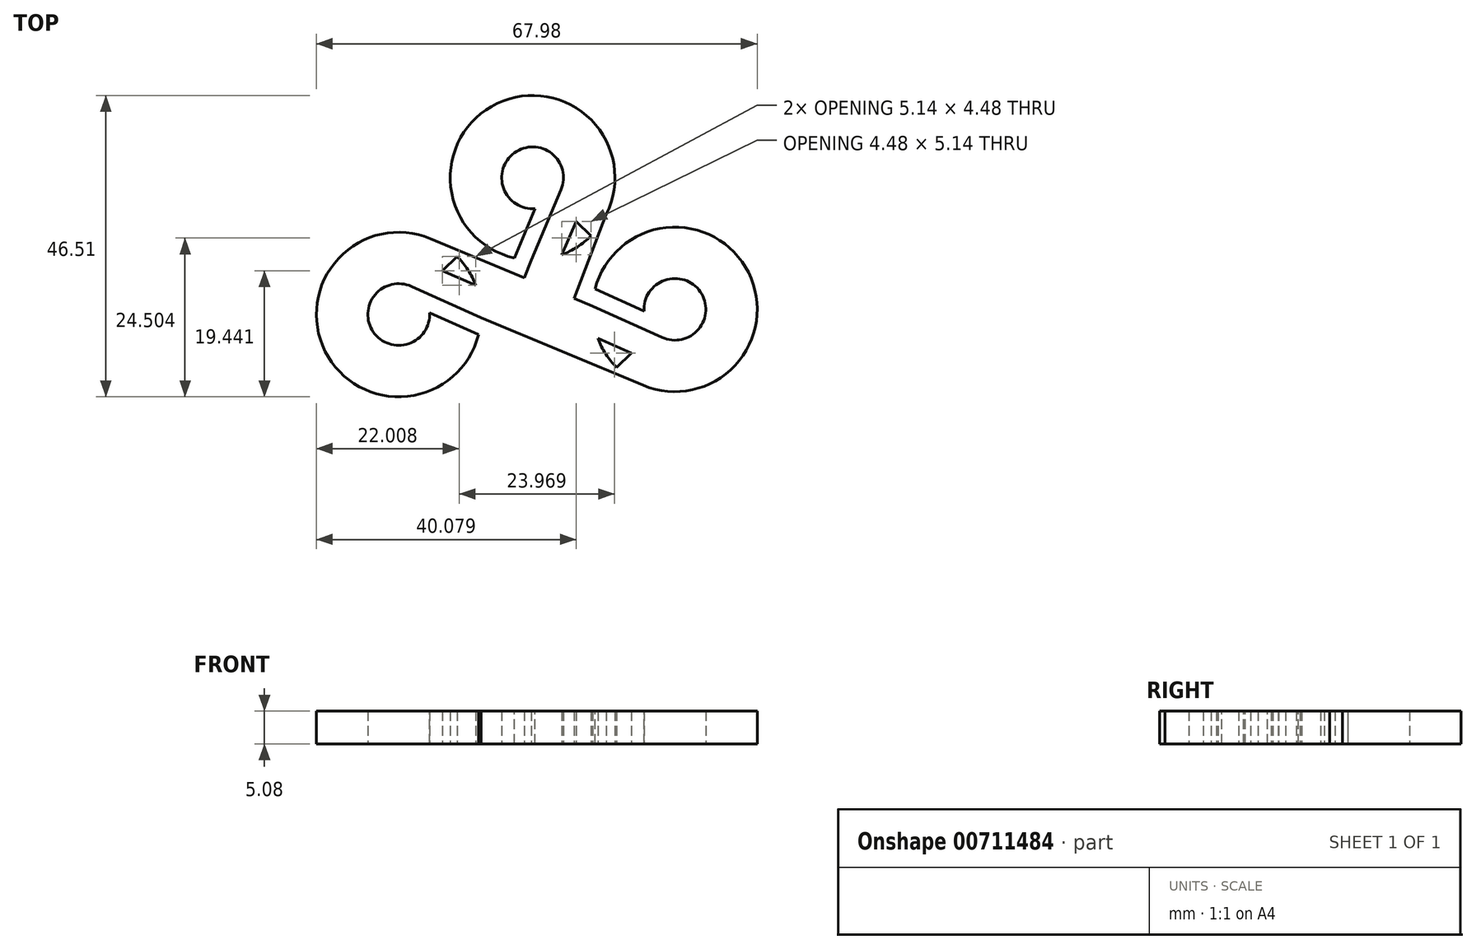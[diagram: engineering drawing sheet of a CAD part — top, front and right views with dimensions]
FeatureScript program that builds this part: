
annotation { "Feature Type Name" : "Feature", "Feature Type Description" : "" }
export const myFeature = defineFeature(function(context is Context, id is Id, definition is map)
    precondition{}
    {
        {
            var Q0;
            Q0=qCreatedBy(makeId("Top.planeOp"),FACE);
            var sketch = newSketch(context, id + "F0", { "sketchPlane" : qUnion([Q0])});
            skCircle(sketch, "E0", {"center": v(0, 0) * mm, "radius": 12.7 * mm});
            skCircle(sketch, "E1", {"center": v(21.94, -20.3) * mm, "radius": 12.7 * mm});
            skCircle(sketch, "E2", {"center": v(-20.64, -21.1) * mm, "radius": 12.7 * mm});
            skLineSegment(sketch, "E3", {"start": v(21.94, -20.3) * mm, "end": v(21.94, -33) * mm});
            skLineSegment(sketch, "E4", {"start": v(0, 0) * mm, "end": v(0, -12.7) * mm});
            skLineSegment(sketch, "E5", {"start": v(0, 0) * mm, "end": v(8.98, -8.98) * mm});
            skLineSegment(sketch, "E6", {"start": v(21.94, -20.3) * mm, "end": v(12.96, -29.29) * mm});
            skCircle(sketch, "E7", {"center": v(21.94, -20.3) * mm, "radius": 4.76 * mm});
            skLineSegment(sketch, "E8", {"start": v(21.94, -20.3) * mm, "end": v(17.45, -24.8) * mm});
            skCircle(sketch, "E9", {"center": v(0, 0) * mm, "radius": 4.76 * mm});
            skLineSegment(sketch, "E10", {"start": v(0, 0) * mm, "end": v(4.5, -4.5) * mm});
            skLineSegment(sketch, "E11", {"start": v(-20.64, -21.1) * mm, "end": v(-11.66, -12.13) * mm});
            skCircle(sketch, "E12", {"center": v(-20.64, -21.1) * mm, "radius": 4.76 * mm});
            skLineSegment(sketch, "E13", {"start": v(-20.64, -21.1) * mm, "end": v(-7.94, -21.1) * mm});
            skLineSegment(sketch, "E14", {"start": v(17.45, -24.8) * mm, "end": v(12.96, -29.29) * mm});
            skLineSegment(sketch, "E15", {"start": v(12.96, -29.29) * mm, "end": v(15.2, -27.04) * mm});
            skLineSegment(sketch, "E16", {"start": v(4.5, -4.5) * mm, "end": v(8.98, -8.98) * mm});
            skLineSegment(sketch, "E17", {"start": v(-16.15, -16.62) * mm, "end": v(-11.66, -12.13) * mm});
            skLineSegment(sketch, "E18", {"start": v(-17.27, -17.74) * mm, "end": v(17.06, -32.03) * mm});
            skLineSegment(sketch, "E19", {"start": v(18.58, -23.68) * mm, "end": v(-15.76, -9.38) * mm});
            skLineSegment(sketch, "E20", {"start": v(3.37, -3.37) * mm, "end": v(-1.24, -15.43) * mm});
            skLineSegment(sketch, "E21", {"start": v(-17.27, -17.74) * mm, "end": v(-13.9, -14.37) * mm});
            skLineSegment(sketch, "E22", {"start": v(-13.9, -14.37) * mm, "end": v(15.2, -27.04) * mm});
            skLineSegment(sketch, "E23", {"start": v(6.74, -6.74) * mm, "end": v(0.65, -20.7) * mm});
            skLineSegment(sketch, "E24", {"start": v(11.39, -5.62) * mm, "end": v(6.42, -18.62) * mm});
            skSolve(sketch);
        }
        {
            var Q0;
            Q0 = qSketchRegion(id + "F0", true);
            var Q1;
            {var subQ0=sQuery(id+"F0.wireOp",EDGE,"yDXB3k3o-TFvE-FYoA-wN1f-QkH4QK7AQUMg");var subQ1=sQuery(id+"F0.wireOp",EDGE,"E0");var subQ2=makeQuery(id+"F0.imprint","INTERSECT",VERTEX,{"derivedFrom":[subQ1,subQ0]});Q1=makeQuery(id+"F0.imprint","IMPRINT",FACE,{"disambiguationData":[TD([[makeQuery(id+"F0.imprint","IMPRINT",EDGE,{"disambiguationData":[TD([[subQ2,-1.0]])],"derivedFrom":subQ1}),1.0]])]});}
            var Q2;
            {var subQ0=sQuery(id+"F0.wireOp",EDGE,"E17");var subQ3=sQuery(id+"F0.wireOp",EDGE,"J90078Zz-WnI3-3mMf-xPuW-VheWCmXxd4jc");var subQ5=makeQuery(id+"F0.imprint","INTERSECT",VERTEX,{"derivedFrom":[subQ0,subQ3]});Q2=makeQuery(id+"F0.imprint","IMPRINT",FACE,{"disambiguationData":[TD([[makeQuery(id+"F0.imprint","IMPRINT",EDGE,{"disambiguationData":[TD([[subQ5,-1.0]])],"derivedFrom":subQ3}),1.0]])]});}
            var Q3;
            {var subQ0=sQuery(id+"F0.wireOp",EDGE,"E16");var subQ3=sQuery(id+"F0.wireOp",EDGE,"qBhyJChg-6HFi-ImKc-3mO0-xAAPeeJnZw3U");var subQ5=makeQuery(id+"F0.imprint","INTERSECT",VERTEX,{"derivedFrom":[subQ0,subQ3]});Q3=makeQuery(id+"F0.imprint","IMPRINT",FACE,{"disambiguationData":[TD([[makeQuery(id+"F0.imprint","IMPRINT",EDGE,{"disambiguationData":[TD([[subQ5,-1.0]])],"derivedFrom":subQ3}),1.0]])]});}
            var Q4;
            {var subQ0=sQuery(id+"F0.wireOp",EDGE,"E15");Q4=makeQuery(id+"F0.imprint","IMPRINT",FACE,{"disambiguationData":[TD([[makeQuery(id+"F0.imprint","IMPRINT",EDGE,{"derivedFrom":subQ0}),1.0]])]});}
            var Q5;
            {var subQ0=sQuery(id+"F0.wireOp",EDGE,"uzKKBWqX-qUkN-Bwqt-uPOb-Zz89Ibqqk1gW");var subQ1=sQuery(id+"F0.wireOp",EDGE,"E2");var subQ2=makeQuery(id+"F0.imprint","INTERSECT",VERTEX,{"derivedFrom":[subQ1,subQ0]});Q5=makeQuery(id+"F0.imprint","IMPRINT",FACE,{"disambiguationData":[TD([[makeQuery(id+"F0.imprint","IMPRINT",EDGE,{"disambiguationData":[TD([[subQ2,-1.0]])],"derivedFrom":subQ1}),-1.0]])]});}
            var Q6;
            {var subQ0=sQuery(id+"F0.wireOp",EDGE,"bYxaBZOP-HbRW-pdFW-15Ub-mmeAeTIA2QFz");Q6=makeQuery(id+"F0.imprint","IMPRINT",FACE,{"disambiguationData":[TD([[makeQuery(id+"F0.imprint","IMPRINT",EDGE,{"derivedFrom":subQ0}),-1.0]])]});}
            var Q7;
            {var subQ0=sQuery(id+"F0.wireOp",EDGE,"uzKKBWqX-qUkN-Bwqt-uPOb-Zz89Ibqqk1gW");var subQ1=sQuery(id+"F0.wireOp",EDGE,"E2");var subQ2=makeQuery(id+"F0.imprint","INTERSECT",VERTEX,{"derivedFrom":[subQ1,subQ0]});Q7=makeQuery(id+"F0.imprint","IMPRINT",FACE,{"disambiguationData":[TD([[makeQuery(id+"F0.imprint","IMPRINT",EDGE,{"disambiguationData":[TD([[subQ2,-1.0]])],"derivedFrom":subQ1}),1.0]])]});}
            var Q8;
            {var subQ0=sQuery(id+"F0.wireOp",EDGE,"Z3ejKgqz-Hqn6-uIZ8-Rk3e-6zc6qRlB8dJ0");Q8=makeQuery(id+"F0.imprint","IMPRINT",FACE,{"disambiguationData":[TD([[makeQuery(id+"F0.imprint","IMPRINT",EDGE,{"derivedFrom":subQ0}),-1.0]])]});}
            var Q9;
            {var subQ1=sQuery(id+"F0.wireOp",EDGE,"E0");var subQ3=sQuery(id+"F0.wireOp",EDGE,"qBhyJChg-6HFi-ImKc-3mO0-xAAPeeJnZw3U");var subQ4=makeQuery(id+"F0.imprint","INTERSECT",VERTEX,{"derivedFrom":[subQ1,subQ3]});Q9=makeQuery(id+"F0.imprint","IMPRINT",FACE,{"disambiguationData":[TD([[makeQuery(id+"F0.imprint","IMPRINT",EDGE,{"disambiguationData":[TD([[subQ4,-1.0]])],"derivedFrom":subQ3}),1.0]])]});}
            var Q10;
            {var subQ3=sQuery(id+"F0.wireOp",EDGE,"E0");var subQ5=sQuery(id+"F0.wireOp",EDGE,"E4");var subQ6=makeQuery(id+"F0.imprint","INTERSECT",VERTEX,{"derivedFrom":[subQ3,subQ5]});Q10=makeQuery(id+"F0.imprint","IMPRINT",FACE,{"disambiguationData":[TD([[makeQuery(id+"F0.imprint","IMPRINT",EDGE,{"disambiguationData":[TD([[subQ6,-1.0]])],"derivedFrom":subQ3}),1.0]])]});}
            var Q11;
            {var subQ0=sQuery(id+"F0.wireOp",EDGE,"yDXB3k3o-TFvE-FYoA-wN1f-QkH4QK7AQUMg");var subQ1=sQuery(id+"F0.wireOp",EDGE,"E0");var subQ2=makeQuery(id+"F0.imprint","INTERSECT",VERTEX,{"derivedFrom":[subQ1,subQ0]});Q11=makeQuery(id+"F0.imprint","IMPRINT",FACE,{"disambiguationData":[TD([[makeQuery(id+"F0.imprint","IMPRINT",EDGE,{"disambiguationData":[TD([[subQ2,-1.0]])],"derivedFrom":subQ1}),-1.0]])]});}
            var Q12;
            {var subQ0=sQuery(id+"F0.wireOp",EDGE,"Z3ejKgqz-Hqn6-uIZ8-Rk3e-6zc6qRlB8dJ0");Q12=makeQuery(id+"F0.imprint","IMPRINT",FACE,{"disambiguationData":[TD([[makeQuery(id+"F0.imprint","IMPRINT",EDGE,{"derivedFrom":subQ0}),1.0]])]});}
            var Q13;
            {var subQ0=sQuery(id+"F0.wireOp",EDGE,"6yfvUeka-AtBQ-0gim-mu1m-la48lc1LBtnG");var subQ5=sQuery(id+"F0.wireOp",EDGE,"qBhyJChg-6HFi-ImKc-3mO0-xAAPeeJnZw3U");var subQ6=makeQuery(id+"F0.imprint","INTERSECT",VERTEX,{"derivedFrom":[subQ0,subQ5]});Q13=makeQuery(id+"F0.imprint","IMPRINT",FACE,{"disambiguationData":[TD([[makeQuery(id+"F0.imprint","IMPRINT",EDGE,{"disambiguationData":[TD([[subQ6,1.0]])],"derivedFrom":subQ5}),-1.0]])]});}
            var Q14;
            {var subQ0=sQuery(id+"F0.wireOp",EDGE,"6yfvUeka-AtBQ-0gim-mu1m-la48lc1LBtnG");var subQ5=sQuery(id+"F0.wireOp",EDGE,"qBhyJChg-6HFi-ImKc-3mO0-xAAPeeJnZw3U");var subQ6=makeQuery(id+"F0.imprint","INTERSECT",VERTEX,{"derivedFrom":[subQ0,subQ5]});Q14=makeQuery(id+"F0.imprint","IMPRINT",FACE,{"disambiguationData":[TD([[makeQuery(id+"F0.imprint","IMPRINT",EDGE,{"disambiguationData":[TD([[subQ6,1.0]])],"derivedFrom":subQ5}),1.0]])]});}
            var Q15;
            {var subQ0=sQuery(id+"F0.wireOp",EDGE,"z5MUbxWM-Vo3r-AQEv-g91w-RWlkdqbgf4P1");Q15=makeQuery(id+"F0.imprint","IMPRINT",FACE,{"disambiguationData":[TD([[makeQuery(id+"F0.imprint","IMPRINT",EDGE,{"derivedFrom":subQ0}),-1.0]])]});}
            var Q16;
            {var subQ1=sQuery(id+"F0.wireOp",EDGE,"E12");var subQ3=sQuery(id+"F0.wireOp",EDGE,"E13");var subQ4=makeQuery(id+"F0.imprint","INTERSECT",VERTEX,{"derivedFrom":[subQ1,subQ3]});Q16=makeQuery(id+"F0.imprint","IMPRINT",FACE,{"disambiguationData":[TD([[makeQuery(id+"F0.imprint","IMPRINT",EDGE,{"disambiguationData":[TD([[subQ4,-1.0]])],"derivedFrom":subQ3}),1.0]])]});}
            var Q17;
            {var subQ3=sQuery(id+"F0.wireOp",EDGE,"E2");var subQ7=sQuery(id+"F0.wireOp",EDGE,"E13");var subQ8=makeQuery(id+"F0.imprint","INTERSECT",VERTEX,{"derivedFrom":[subQ3,subQ7]});Q17=makeQuery(id+"F0.imprint","IMPRINT",FACE,{"disambiguationData":[TD([[makeQuery(id+"F0.imprint","IMPRINT",EDGE,{"disambiguationData":[TD([[subQ8,-1.0]])],"derivedFrom":subQ3}),1.0]])]});}
            var Q18;
            {var subQ5=sQuery(id+"F0.wireOp",EDGE,"E14");Q18=makeQuery(id+"F0.imprint","IMPRINT",FACE,{"disambiguationData":[TD([[makeQuery(id+"F0.imprint","IMPRINT",EDGE,{"derivedFrom":subQ5}),-1.0]])]});}
            var Q19;
            {var subQ0=sQuery(id+"F0.wireOp",EDGE,"NG6Fn4Pl-cfwn-nJXz-Nv7R-ltP6G86gKaW2");var subQ1=sQuery(id+"F0.wireOp",EDGE,"E1");var subQ2=makeQuery(id+"F0.imprint","INTERSECT",VERTEX,{"derivedFrom":[subQ1,subQ0]});Q19=makeQuery(id+"F0.imprint","IMPRINT",FACE,{"disambiguationData":[TD([[makeQuery(id+"F0.imprint","IMPRINT",EDGE,{"disambiguationData":[TD([[subQ2,-1.0]])],"derivedFrom":subQ1}),-1.0]])]});}
            var Q20;
            {var subQ0=sQuery(id+"F0.wireOp",EDGE,"bYxaBZOP-HbRW-pdFW-15Ub-mmeAeTIA2QFz");Q20=makeQuery(id+"F0.imprint","IMPRINT",FACE,{"disambiguationData":[TD([[makeQuery(id+"F0.imprint","IMPRINT",EDGE,{"derivedFrom":subQ0}),1.0]])]});}
            var Q21;
            {var subQ1=sQuery(id+"F0.wireOp",EDGE,"z5MUbxWM-Vo3r-AQEv-g91w-RWlkdqbgf4P1");Q21=makeQuery(id+"F0.imprint","IMPRINT",FACE,{"disambiguationData":[TD([[makeQuery(id+"F0.imprint","IMPRINT",EDGE,{"derivedFrom":subQ1}),1.0]])]});}
            var Q22;
            {var subQ0=sQuery(id+"F0.wireOp",EDGE,"eJoCJf4v-nHHx-lm19-L27D-6VjAbPNY3byg");var subQ1=sQuery(id+"F0.wireOp",EDGE,"E2");var subQ2=makeQuery(id+"F0.imprint","INTERSECT",VERTEX,{"derivedFrom":[subQ1,subQ0]});Q22=makeQuery(id+"F0.imprint","IMPRINT",FACE,{"disambiguationData":[TD([[makeQuery(id+"F0.imprint","IMPRINT",EDGE,{"disambiguationData":[TD([[subQ2,-1.0]])],"derivedFrom":subQ1}),1.0]])]});}
            var Q23;
            {var subQ0=sQuery(id+"F0.wireOp",EDGE,"E9");var subQ1=sQuery(id+"F0.wireOp",EDGE,"E4");var subQ2=makeQuery(id+"F0.imprint","INTERSECT",VERTEX,{"derivedFrom":[subQ1,subQ0]});Q23=makeQuery(id+"F0.imprint","IMPRINT",FACE,{"disambiguationData":[TD([[makeQuery(id+"F0.imprint","IMPRINT",EDGE,{"disambiguationData":[TD([[subQ2,-1.0]])],"derivedFrom":subQ1}),1.0]])]});}
            var Q24;
            {var subQ0=sQuery(id+"F0.wireOp",EDGE,"E17");Q24=makeQuery(id+"F0.imprint","IMPRINT",FACE,{"disambiguationData":[TD([[makeQuery(id+"F0.imprint","IMPRINT",EDGE,{"derivedFrom":subQ0}),-1.0]])]});}
            var Q25;
            {var subQ0=sQuery(id+"F0.wireOp",EDGE,"E16");var subQ1=sQuery(id+"F0.wireOp",EDGE,"E0");var subQ2=makeQuery(id+"F0.imprint","INTERSECT",VERTEX,{"derivedFrom":[subQ1,subQ0]});Q25=makeQuery(id+"F0.imprint","IMPRINT",FACE,{"disambiguationData":[TD([[makeQuery(id+"F0.imprint","IMPRINT",EDGE,{"disambiguationData":[TD([[subQ2,1.0]])],"derivedFrom":subQ1}),1.0]])]});}
            extrude(context, id + "F1", {"entities" : qUnion([Q0, Q1, Q2, Q3, Q4, Q5, Q6, Q7, Q8, Q9, Q10, Q11, Q12, Q13, Q14, Q15, Q16, Q17, Q18, Q19, Q20, Q21, Q22, Q23, Q24, Q25]), "depth" : 5.08 * mm, "offsetDistance" : 25.4 * mm});
        }
        {
            var Q0;
            Q0=makeQuery(id+"F1.opExtrude","CAP_FACE",FACE,{"disambiguationData":[OSD([sQuery(id+"F0.wireOp",EDGE,"E0"),sQuery(id+"F0.wireOp",EDGE,"E1"),sQuery(id+"F0.wireOp",EDGE,"E2"),sQuery(id+"F0.wireOp",EDGE,"VeAweMac-LZ9O-rFIa-PTyz-U5xl3IZNd5pn"),sQuery(id+"F0.wireOp",EDGE,"E7"),sQuery(id+"F0.wireOp",EDGE,"NG6Fn4Pl-cfwn-nJXz-Nv7R-ltP6G86gKaW2"),sQuery(id+"F0.wireOp",EDGE,"E9"),sQuery(id+"F0.wireOp",EDGE,"yDXB3k3o-TFvE-FYoA-wN1f-QkH4QK7AQUMg"),sQuery(id+"F0.wireOp",EDGE,"6yfvUeka-AtBQ-0gim-mu1m-la48lc1LBtnG"),sQuery(id+"F0.wireOp",EDGE,"E12"),sQuery(id+"F0.wireOp",EDGE,"uzKKBWqX-qUkN-Bwqt-uPOb-Zz89Ibqqk1gW"),sQuery(id+"F0.wireOp",EDGE,"z5MUbxWM-Vo3r-AQEv-g91w-RWlkdqbgf4P1"),sQuery(id+"F0.wireOp",EDGE,"qBhyJChg-6HFi-ImKc-3mO0-xAAPeeJnZw3U"),sQuery(id+"F0.wireOp",EDGE,"Vy6klFHD-ql6F-NG0b-UYJ5-acndccB01QWS"),sQuery(id+"F0.wireOp",EDGE,"OdPr5M7K-QP7o-Xsb9-YXNN-OMWYOfSv6xGX"),sQuery(id+"F0.wireOp",EDGE,"tfzjCEgK-RNZ7-z4IH-43NG-UBwa0SwhfyJe")])],"isStart":false});
            var sketch = newSketch(context, id + "F2", { "sketchPlane" : qUnion([Q0])});
            skLineSegment(sketch, "E25", {"start": v(-0.2, -12.7) * mm, "end": v(4.39, -1.86) * mm});
            skLineSegment(sketch, "E26", {"start": v(-2.82, -12.38) * mm, "end": v(0.4, -4.75) * mm});
            skLineSegment(sketch, "E27", {"start": v(-7.95, -21.62) * mm, "end": v(-18.68, -16.77) * mm});
            skLineSegment(sketch, "E28", {"start": v(-15.88, -20.82) * mm, "end": v(-8.33, -24.24) * mm});
            skLineSegment(sketch, "E29", {"start": v(9.25, -19.8) * mm, "end": v(19.98, -24.65) * mm});
            skLineSegment(sketch, "E30", {"start": v(9.63, -17.18) * mm, "end": v(17.19, -20.6) * mm});
            skSolve(sketch);
        }
        {
            var Q0;
            {var subQ0=sQuery(id+"F2.wireOp",EDGE,"E27");Q0=makeQuery(id+"F2.imprint","IMPRINT",FACE,{"disambiguationData":[TD([[makeQuery(id+"F2.imprint","IMPRINT",EDGE,{"derivedFrom":subQ0}),1.0]])]});}
            var Q1;
            {var subQ0=sQuery(id+"F2.wireOp",EDGE,"E25");Q1=makeQuery(id+"F2.imprint","IMPRINT",FACE,{"disambiguationData":[TD([[makeQuery(id+"F2.imprint","IMPRINT",EDGE,{"derivedFrom":subQ0}),1.0]])]});}
            var Q2;
            {var subQ0=sQuery(id+"F2.wireOp",EDGE,"E29");Q2=makeQuery(id+"F2.imprint","IMPRINT",FACE,{"disambiguationData":[TD([[makeQuery(id+"F2.imprint","IMPRINT",EDGE,{"derivedFrom":subQ0}),1.0]])]});}
            extrude(context, id + "F3", {"entities" : qUnion([Q0, Q1, Q2]), "operationType" : NewBodyOperationType.REMOVE, "oppositeDirection" : true, "depth" : 25.4 * mm, "offsetDistance" : 25.4 * mm});
        }
    });
